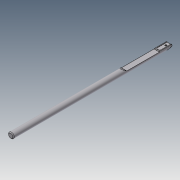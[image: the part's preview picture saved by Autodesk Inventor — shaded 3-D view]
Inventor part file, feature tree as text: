
AUTODESK INVENTOR PART (.ipt)
format: ipt  version: 2018.3 (Build 223284000, 284)  size: 175,616 bytes
history: native  units: in
note: dims shown in document units (in); Inventor stores cm internally (conversion verified against a paired STEP export)
features: sketch x9, extrude x7, chamfer x3, hole x1, fillet x1
ambient origin geometry x8: Origin, YZ Plane, XZ Plane, XY Plane, X Axis, Y Axis, Z Axis, Center Point
bodies: Solid1 (feature_tree)
feature tree (21):
  extrude  "Extrusion1"  Depth=7.0in TaperAngle=0.0deg
  sketch  "Sketch2"  dims[d6=0.055in d7=0.5in d8=0.0in]
  extrude  "Extrusion3"  Depth=0.5in TaperAngle=0.0deg
  extrude  "Extrusion4"  Depth=0.166in
  hole  "Hole1"  [1 undecoded]
  extrude  "Extrusion5"  TaperAngle=30.0deg  [1 undecoded]
  chamfer  "Chamfer1"  Distance=0.5in
  chamfer  "Chamfer2"  Distance=0.01in Angle=45.0deg
  chamfer  "Chamfer3"  Distance=0.01in Angle=45.0deg
  extrude  "Extrusion7"  Depth=0.018in
  extrude  "Extrusion8"  TaperAngle=0.0deg  [1 undecoded]
  sketch  "Sketch8"  dims[d15=0.079in d16=0.197in d17=0.375in d18=0.25in d19=0.5635in d20=0.299in d21=0.8108in d23=30.0deg d24=0.5in d25=0.0in d26=0.01in d27=0.015in d28=45.0deg d29=0.01in d30=0.015in d31=45.0deg]
  sketch  "Sketch9"  dims[d32=0.03in d33=0.015in d34=45.0deg d40=0.018in]
  sketch  "Sketch10"  dims[d41=2.0in d42=0.0in d43=0.0in d44=0.05in]
  fillet  "Fillet3"  Radius=0.05in
  extrude  "Extrusion10"  Depth=0.02in TaperAngle=0.0deg
  sketch  "Sketch1"  dims[d0=0.25in d1=7.0in d2=0.0in]
  sketch  "Sketch3"  dims[d9=60.0deg d10=0.166in]
  sketch  "Sketch4"  dims[d11=0.022in d12=0.5in d13=0.0in]
  sketch  "Sketch6"  dims[d14=0.15in]
  sketch  "Sketch11"  dims[d45=0.35in d46=0.02in d47=0.0in d53=0.04in d56=0.005in d57=0.55in d58=0.005in d59=30.0deg d60=0.024in d61=0.25in d62=0.0in]
note: 3 required parameter values undecoded (feature->parameter linkage not recoverable at this tier; creation-order binding heuristic only, values carry confidence <= 0.55)
